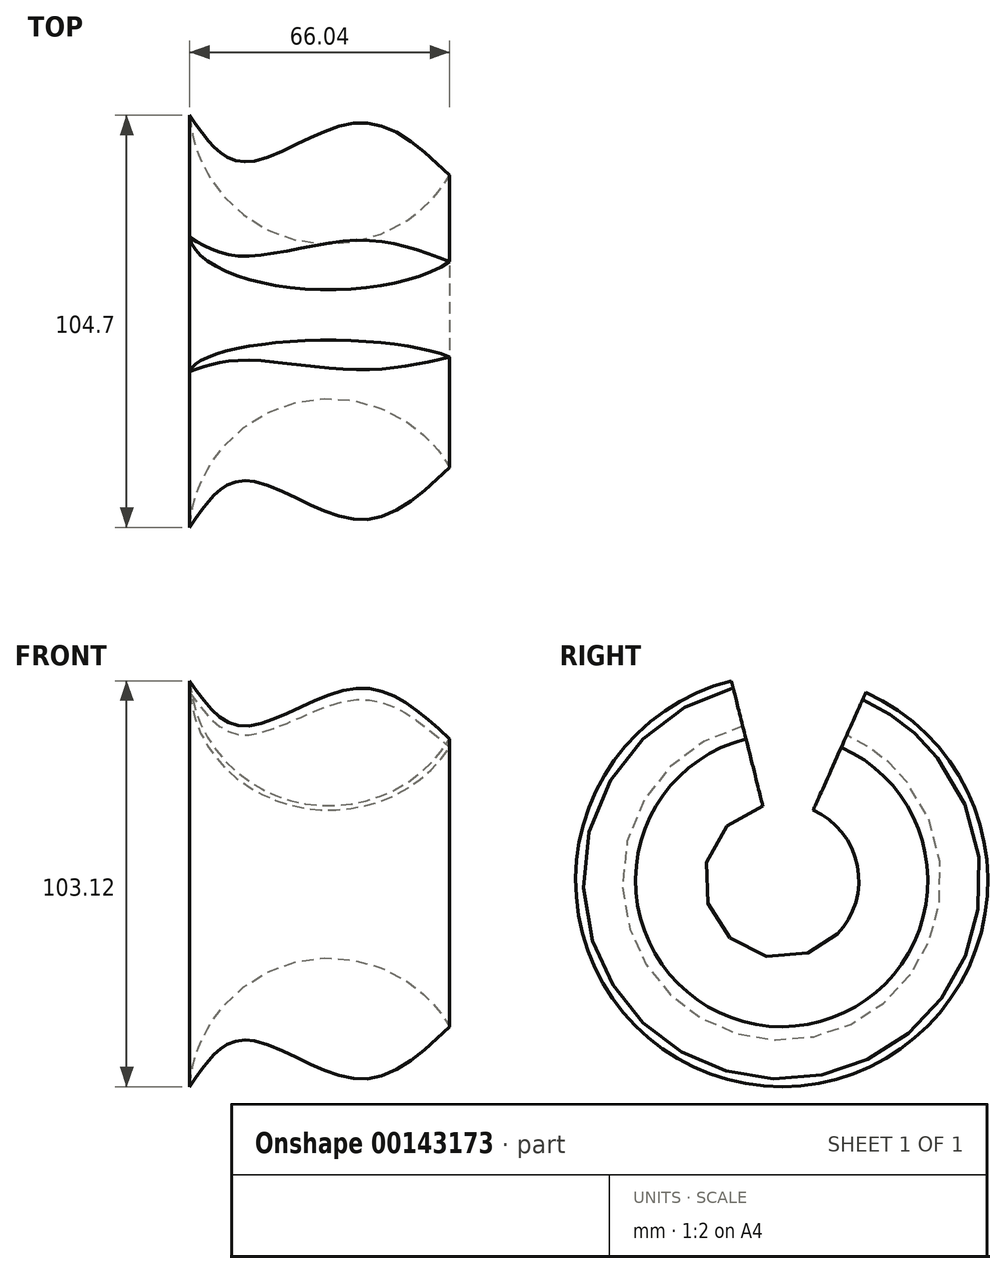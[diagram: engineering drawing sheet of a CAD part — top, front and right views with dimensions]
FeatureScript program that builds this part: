
annotation { "Feature Type Name" : "Feature", "Feature Type Description" : "" }
export const myFeature = defineFeature(function(context is Context, id is Id, definition is map)
    precondition{}
    {
        {
            var Q0;
            Q0=qCreatedBy(makeId("Front.planeOp"),FACE);
            var sketch = newSketch(context, id + "F0", { "sketchPlane" : qUnion([Q0])});
            skFitSpline(sketch, "E0", {"points": [v(0, 52.35) * mm, v(13.83, 40.5) * mm, v(42.33, 50.38) * mm, v(66.04, 37.11) * mm], "startDerivative": vector(41.06, -61.66) * mm, "endDerivative": vector(63.43, -60.23) * mm});
            skArc(sketch, "E1", {"start": v(0, 52.35) * mm, "mid": v(27.43, 20.52) * mm, "end": v(66.04, 37.11) * mm});
            skLineSegment(sketch, "E2", {"start": v(0, 0) * mm, "end": v(76.2, 0) * mm, "construction": true});
            skSolve(sketch);
        }
        {
            var Q0;
            Q0 = qSketchRegion(id + "F0", true);
            var Q1;
            Q1=sQuery(id+"F0.wireOp",EDGE,"E2");
            revolve(context, id + "F1", {"entities" : qUnion([Q0]), "axis" : qUnion([Q1]), "revolveType" : RevolveType.FULL});
        }
        {
            var Q0;
            Q0=qCreatedBy(makeId("Right.planeOp"),FACE);
            var sketch = newSketch(context, id + "F2", { "sketchPlane" : qUnion([Q0])});
            skCircle(sketch, "E3.0", {"center": v(0, 0) * mm, "radius": 52.35 * mm, "construction": true});
            skLineSegment(sketch, "E4", {"start": v(0, 0) * mm, "end": v(21.36, 47.8) * mm});
            skLineSegment(sketch, "E5", {"start": v(0, 0) * mm, "end": v(-12.79, 50.77) * mm});
            skArc(sketch, "E6", {"start": v(21.36, 47.8) * mm, "mid": v(4.54, 52.16) * mm, "end": v(-12.79, 50.77) * mm});
            skSolve(sketch);
        }
        {
            var Q0;
            Q0 = qSketchRegion(id + "F2", true);
            extrude(context, id + "F3", {"entities" : qUnion([Q0]), "operationType" : NewBodyOperationType.REMOVE, "depth" : 127 * mm});
        }
    });
